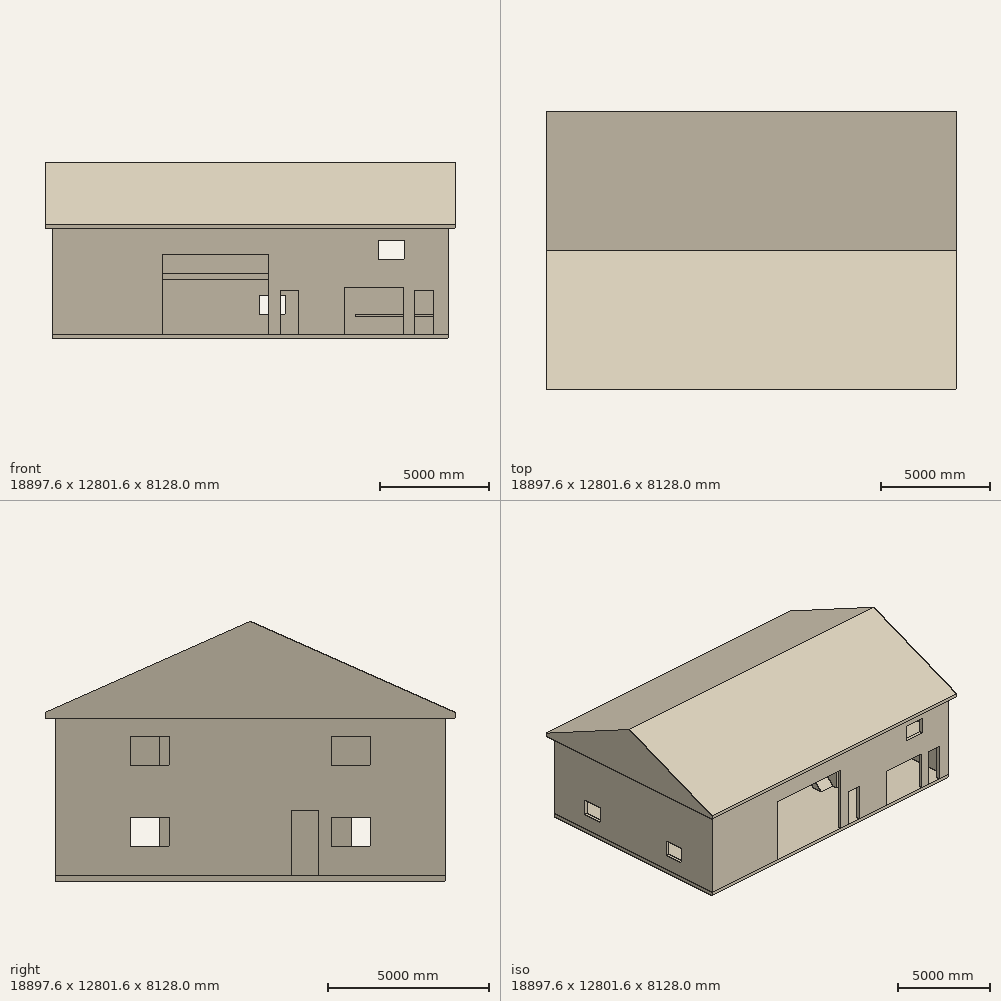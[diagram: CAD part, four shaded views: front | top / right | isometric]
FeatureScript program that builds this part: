
annotation { "Feature Type Name" : "Feature", "Feature Type Description" : "" }
export const myFeature = defineFeature(function(context is Context, id is Id, definition is map)
    precondition{}
    {
        {
            var Q0;
            Q0=qCreatedBy(makeId("Top.planeOp"),FACE);
            var sketch = newSketch(context, id + "F0", { "sketchPlane" : qUnion([Q0])});
            skLineSegment(sketch, "E0.bottom", {"start": v(-9144, 6096) * mm, "end": v(9144, 6096) * mm});
            skLineSegment(sketch, "E0.top", {"start": v(-9144, -6096) * mm, "end": v(9144, -6096) * mm});
            skLineSegment(sketch, "E0.left", {"start": v(-9144, 6096) * mm, "end": v(-9144, -6096) * mm});
            skLineSegment(sketch, "E0.right", {"start": v(9144, 6096) * mm, "end": v(9144, -6096) * mm});
            skLineSegment(sketch, "E1", {"start": v(-9144, 6096) * mm, "end": v(9144, -6096) * mm, "construction": true});
            skSolve(sketch);
        }
        {
            var Q0;
            Q0=makeQuery(id+"F0.imprint","IMPRINT",FACE,{"disambiguationData":[TD([[makeQuery(id+"F0.imprint","IMPRINT",EDGE,{"derivedFrom":sQuery(id+"F0.wireOp",EDGE,"E0.bottom")}),-1.0]])]});
            extrude(context, id + "F1", {"entities" : qUnion([Q0]), "depth" : 203.2 * mm, "offsetDistance" : 25.4 * mm});
        }
        {
            var Q0;
            Q0=makeQuery(id+"F1.opExtrude","CAP_FACE",FACE,{"disambiguationData":[OSD([sQuery(id+"F0.wireOp",EDGE,"E0.bottom"),sQuery(id+"F0.wireOp",EDGE,"E0.top"),sQuery(id+"F0.wireOp",EDGE,"E0.left"),sQuery(id+"F0.wireOp",EDGE,"E0.right")])],"isStart":false});
            var sketch = newSketch(context, id + "F2", { "sketchPlane" : qUnion([Q0])});
            skLineSegment(sketch, "E2.0", {"start": v(-9144, 6096) * mm, "end": v(9144, 6096) * mm});
            skLineSegment(sketch, "E2.1", {"start": v(-9144, 6096) * mm, "end": v(-9144, -6096) * mm});
            skLineSegment(sketch, "E2.2", {"start": v(-9144, -6096) * mm, "end": v(9144, -6096) * mm});
            skLineSegment(sketch, "E2.3", {"start": v(9144, 6096) * mm, "end": v(9144, -6096) * mm});
            skLineSegment(sketch, "E3.0", {"start": v(-8940.8, 5892.8) * mm, "end": v(8940.8, 5892.8) * mm});
            skLineSegment(sketch, "E3.1", {"start": v(-8940.8, 5892.8) * mm, "end": v(-8940.8, -5892.8) * mm});
            skLineSegment(sketch, "E3.2", {"start": v(-8940.8, -5892.8) * mm, "end": v(8940.8, -5892.8) * mm});
            skLineSegment(sketch, "E3.3", {"start": v(8940.8, 5892.8) * mm, "end": v(8940.8, -5892.8) * mm});
            skSolve(sketch);
        }
        {
            var Q0;
            Q0 = qSketchRegion(id + "F2", true);
            extrude(context, id + "F3", {"entities" : qUnion([Q0]), "depth" : 4876.8 * mm, "offsetDistance" : 25.4 * mm});
        }
        {
            var Q0;
            Q0=qCreatedBy(makeId("Right.planeOp"),FACE);
            var sketch = newSketch(context, id + "F4", { "sketchPlane" : qUnion([Q0])});
            skLineSegment(sketch, "E4.0", {"start": v(6400.8, 5080) * mm, "end": v(-6400.8, 5080) * mm});
            skLineSegment(sketch, "E5", {"start": v(-6400.8, 5080) * mm, "end": v(-6400.8, 5283.2) * mm});
            skLineSegment(sketch, "E6", {"start": v(-6400.8, 5283.2) * mm, "end": v(0, 8128) * mm});
            skLineSegment(sketch, "E7", {"start": v(0, 8128) * mm, "end": v(6400.8, 5283.2) * mm});
            skLineSegment(sketch, "E8", {"start": v(6400.8, 5283.2) * mm, "end": v(6400.8, 5080) * mm});
            skSolve(sketch);
        }
        {
            var Q0;
            Q0 = qSketchRegion(id + "F4", true);
            var Q1;
            Q1=makeQuery(id+"F3.opExtrude","SWEPT_FACE",FACE,{"disambiguationData":[OSD([sQuery(id+"F2.wireOp",EDGE,"E2.3")])]});
            var Q2;
            Q2=makeQuery(id+"F3.opExtrude","SWEPT_FACE",FACE,{"disambiguationData":[OSD([sQuery(id+"F2.wireOp",EDGE,"E2.1")])]});
            extrude(context, id + "F5", {"entities" : qUnion([Q0]), "endBound" : BoundingType.UP_TO_SURFACE, "depth" : 25.4 * mm, "endBoundEntityFace" : qUnion([Q1]), "hasOffset" : true, "offsetDistance" : -304.8 * mm, "hasSecondDirection" : true, "secondDirectionBound" : SecondDirectionBoundingType.UP_TO_SURFACE, "secondDirectionOppositeDirection" : true, "secondDirectionDepth" : 25.4 * mm, "secondDirectionBoundEntityFace" : qUnion([Q2]), "hasSecondDirectionOffset" : true, "secondDirectionOffsetDistance" : -304.8 * mm});
        }
        {
            var Q0;
            Q0=makeQuery(id+"F1.opExtrude","CAP_FACE",FACE,{"disambiguationData":[OSD([sQuery(id+"F0.wireOp",EDGE,"E0.bottom"),sQuery(id+"F0.wireOp",EDGE,"E0.top"),sQuery(id+"F0.wireOp",EDGE,"E0.left"),sQuery(id+"F0.wireOp",EDGE,"E0.right")])],"isStart":false});
            var sketch = newSketch(context, id + "F6", { "sketchPlane" : qUnion([Q0])});
            skLineSegment(sketch, "E9", {"start": v(3759.2, -5892.8) * mm, "end": v(3759.2, 5892.8) * mm});
            skLineSegment(sketch, "E10.0", {"start": v(3911.6, -5892.8) * mm, "end": v(3911.6, 203.2) * mm});
            skLineSegment(sketch, "E11", {"start": v(3911.6, 355.6) * mm, "end": v(8940.8, 355.6) * mm});
            skLineSegment(sketch, "E12.0", {"start": v(3911.6, 203.2) * mm, "end": v(8940.8, 203.2) * mm});
            skLineSegment(sketch, "E13.trimOffspring", {"start": v(3911.6, 355.6) * mm, "end": v(3911.6, 5892.8) * mm});
            skLineSegment(sketch, "E14", {"start": v(3759.2, -5892.8) * mm, "end": v(3911.6, -5892.8) * mm});
            skLineSegment(sketch, "E15", {"start": v(3759.2, 5892.8) * mm, "end": v(3911.6, 5892.8) * mm});
            skLineSegment(sketch, "E16", {"start": v(8940.8, 355.6) * mm, "end": v(8940.8, 203.2) * mm});
            skSolve(sketch);
        }
        {
            var Q0;
            Q0 = qSketchRegion(id + "F6", true);
            extrude(context, id + "F7", {"entities" : qUnion([Q0]), "depth" : 2336.8 * mm, "offsetDistance" : 25.4 * mm});
        }
        {
            var Q0;
            Q0=makeQuery(id+"F7.opExtrude","CAP_FACE",FACE,{"disambiguationData":[OSD([sQuery(id+"F6.wireOp",EDGE,"E9"),sQuery(id+"F6.wireOp",EDGE,"E10.0"),sQuery(id+"F6.wireOp",EDGE,"E11"),sQuery(id+"F6.wireOp",EDGE,"E12.0"),sQuery(id+"F6.wireOp",EDGE,"E13.trimOffspring"),sQuery(id+"F6.wireOp",EDGE,"E14"),sQuery(id+"F6.wireOp",EDGE,"E15"),sQuery(id+"F6.wireOp",EDGE,"E16")])],"isStart":false});
            var sketch = newSketch(context, id + "F8", { "sketchPlane" : qUnion([Q0])});
            skLineSegment(sketch, "E17.0", {"start": v(3759.2, -5892.8) * mm, "end": v(3759.2, 5892.8) * mm});
            skLineSegment(sketch, "E18.0", {"start": v(8940.8, 5892.8) * mm, "end": v(8940.8, -5892.8) * mm});
            skLineSegment(sketch, "E19.0", {"start": v(3759.2, 5892.8) * mm, "end": v(8940.8, 5892.8) * mm});
            skLineSegment(sketch, "E20.0", {"start": v(3759.2, -5892.8) * mm, "end": v(8940.8, -5892.8) * mm});
            skPoint(sketch, "E21.orphan", {"position": v(-8940.8, -5892.8) * mm});
            skPoint(sketch, "E22.orphan", {"position": v(-8940.8, 5892.8) * mm});
            skSolve(sketch);
        }
        {
            var Q0;
            Q0 = qSketchRegion(id + "F8", true);
            extrude(context, id + "F9", {"entities" : qUnion([Q0]), "depth" : 203.2 * mm, "offsetDistance" : 25.4 * mm});
        }
        {
            var Q0;
            Q0=makeQuery(id+"F3.opExtrude","SWEPT_FACE",FACE,{"disambiguationData":[OSD([sQuery(id+"F2.wireOp",EDGE,"E2.2")])]});
            var sketch = newSketch(context, id + "F10", { "sketchPlane" : qUnion([Q0])});
            skLineSegment(sketch, "E23.bottom", {"start": v(-4064, 203.2) * mm, "end": v(812.8, 203.2) * mm});
            skLineSegment(sketch, "E23.top", {"start": v(-4064, 3860.8) * mm, "end": v(812.8, 3860.8) * mm});
            skLineSegment(sketch, "E23.left", {"start": v(-4064, 203.2) * mm, "end": v(-4064, 3860.8) * mm});
            skLineSegment(sketch, "E23.right", {"start": v(812.8, 203.2) * mm, "end": v(812.8, 3860.8) * mm});
            skLineSegment(sketch, "E24.bottom", {"start": v(1371.6, 203.2) * mm, "end": v(2235.2, 203.2) * mm});
            skLineSegment(sketch, "E24.top", {"start": v(1371.6, 2235.2) * mm, "end": v(2235.2, 2235.2) * mm});
            skLineSegment(sketch, "E24.left", {"start": v(1371.6, 203.2) * mm, "end": v(1371.6, 2235.2) * mm});
            skLineSegment(sketch, "E24.right", {"start": v(2235.2, 203.2) * mm, "end": v(2235.2, 2235.2) * mm});
            skLineSegment(sketch, "E25.bottom", {"start": v(4318, 203.2) * mm, "end": v(7061.2, 203.2) * mm});
            skLineSegment(sketch, "E25.top", {"start": v(4318, 2336.8) * mm, "end": v(7061.2, 2336.8) * mm});
            skLineSegment(sketch, "E25.left", {"start": v(4318, 203.2) * mm, "end": v(4318, 2336.8) * mm});
            skLineSegment(sketch, "E25.right", {"start": v(7061.2, 203.2) * mm, "end": v(7061.2, 2336.8) * mm});
            skLineSegment(sketch, "E26.bottom", {"start": v(7569.2, 203.2) * mm, "end": v(8432.8, 203.2) * mm});
            skLineSegment(sketch, "E26.top", {"start": v(7569.2, 2235.2) * mm, "end": v(8432.8, 2235.2) * mm});
            skLineSegment(sketch, "E26.left", {"start": v(7569.2, 203.2) * mm, "end": v(7569.2, 2235.2) * mm});
            skLineSegment(sketch, "E26.right", {"start": v(8432.8, 203.2) * mm, "end": v(8432.8, 2235.2) * mm});
            skLineSegment(sketch, "E27.bottom", {"start": v(5892.8, 4546.6) * mm, "end": v(7112, 4546.6) * mm});
            skLineSegment(sketch, "E27.top", {"start": v(5892.8, 3632.2) * mm, "end": v(7112, 3632.2) * mm});
            skLineSegment(sketch, "E27.left", {"start": v(5892.8, 4546.6) * mm, "end": v(5892.8, 3632.2) * mm});
            skLineSegment(sketch, "E27.right", {"start": v(7112, 4546.6) * mm, "end": v(7112, 3632.2) * mm});
            skSolve(sketch);
        }
        {
            var Q0;
            Q0 = qSketchRegion(id + "F10", true);
            extrude(context, id + "F11", {"entities" : qUnion([Q0]), "operationType" : NewBodyOperationType.REMOVE, "endBound" : BoundingType.UP_TO_NEXT, "oppositeDirection" : true, "depth" : 25.4 * mm, "offsetDistance" : 25.4 * mm});
        }
        {
            var Q0;
            Q0=makeQuery(id+"F3.opExtrude","SWEPT_FACE",FACE,{"disambiguationData":[OSD([sQuery(id+"F2.wireOp",EDGE,"E2.3")])]});
            var sketch = newSketch(context, id + "F12", { "sketchPlane" : qUnion([Q0])});
            skLineSegment(sketch, "E28.bottom", {"start": v(-5588, 203.2) * mm, "end": v(-4724.4, 203.2) * mm, "construction": true});
            skLineSegment(sketch, "E28.top", {"start": v(-5588, 2235.2) * mm, "end": v(-4724.4, 2235.2) * mm, "construction": true});
            skLineSegment(sketch, "E28.left", {"start": v(-5588, 203.2) * mm, "end": v(-5588, 2235.2) * mm, "construction": true});
            skLineSegment(sketch, "E28.right", {"start": v(-4724.4, 203.2) * mm, "end": v(-4724.4, 2235.2) * mm, "construction": true});
            skLineSegment(sketch, "E29.bottom", {"start": v(1270, 203.2) * mm, "end": v(2133.6, 203.2) * mm});
            skLineSegment(sketch, "E29.top", {"start": v(1270, 2235.2) * mm, "end": v(2133.6, 2235.2) * mm});
            skLineSegment(sketch, "E29.left", {"start": v(1270, 203.2) * mm, "end": v(1270, 2235.2) * mm});
            skLineSegment(sketch, "E29.right", {"start": v(2133.6, 203.2) * mm, "end": v(2133.6, 2235.2) * mm});
            skSolve(sketch);
        }
        {
            var Q0;
            Q0 = qSketchRegion(id + "F12", true);
            extrude(context, id + "F13", {"entities" : qUnion([Q0]), "operationType" : NewBodyOperationType.REMOVE, "endBound" : BoundingType.UP_TO_NEXT, "oppositeDirection" : true, "depth" : 25.4 * mm, "offsetDistance" : 25.4 * mm});
        }
        {
            var Q0;
            Q0=makeQuery(id+"F7.opExtrude","SWEPT_FACE",FACE,{"disambiguationData":[OSD([sQuery(id+"F6.wireOp",EDGE,"E9")])]});
            var sketch = newSketch(context, id + "F14", { "sketchPlane" : qUnion([Q0])});
            skLineSegment(sketch, "E30", {"start": v(1965.26, 203.2) * mm, "end": v(-371.54, 2540) * mm});
            skLineSegment(sketch, "E31", {"start": v(0, 2743.2) * mm, "end": v(2540, 203.2) * mm});
            skLineSegment(sketch, "E32", {"start": v(-574.74, 2743.2) * mm, "end": v(0, 2743.2) * mm});
            skLineSegment(sketch, "E33", {"start": v(2540, 203.2) * mm, "end": v(1965.26, 203.2) * mm});
            skLineSegment(sketch, "E34.bottom", {"start": v(2955.8, 203.2) * mm, "end": v(5394.2, 203.2) * mm, "construction": true});
            skLineSegment(sketch, "E34.top", {"start": v(2955.8, 2336.8) * mm, "end": v(5394.2, 2336.8) * mm, "construction": true});
            skLineSegment(sketch, "E34.left", {"start": v(2955.8, 203.2) * mm, "end": v(2955.8, 2336.8) * mm, "construction": true});
            skLineSegment(sketch, "E34.right", {"start": v(5394.2, 203.2) * mm, "end": v(5394.2, 2336.8) * mm, "construction": true});
            skLineSegment(sketch, "E35.bottom", {"start": v(-4403.76, 203.2) * mm, "end": v(-1965.36, 203.2) * mm, "construction": true});
            skLineSegment(sketch, "E35.top", {"start": v(-4403.76, 2336.8) * mm, "end": v(-1965.36, 2336.8) * mm, "construction": true});
            skLineSegment(sketch, "E35.left", {"start": v(-4403.76, 203.2) * mm, "end": v(-4403.76, 2336.8) * mm, "construction": true});
            skLineSegment(sketch, "E35.right", {"start": v(-1965.36, 203.2) * mm, "end": v(-1965.36, 2336.8) * mm, "construction": true});
            skLineSegment(sketch, "E36", {"start": v(-1219.2, 2540) * mm, "end": v(-1219.2, 2743.2) * mm});
            skLineSegment(sketch, "E37", {"start": v(-1219.2, 2743.2) * mm, "end": v(-574.74, 2743.2) * mm});
            skLineSegment(sketch, "E38", {"start": v(-1219.2, 2540) * mm, "end": v(-371.54, 2540) * mm});
            skSolve(sketch);
        }
        {
            var Q0;
            Q0 = qSketchRegion(id + "F14", true);
            extrude(context, id + "F15", {"entities" : qUnion([Q0]), "depth" : 914.4 * mm, "offsetDistance" : 25.4 * mm});
        }
        {
            var Q0;
            Q0=makeQuery(id+"F7.opExtrude","SWEPT_FACE",FACE,{"disambiguationData":[OSD([sQuery(id+"F6.wireOp",EDGE,"E9")])]});
            var sketch = newSketch(context, id + "F16", { "sketchPlane" : qUnion([Q0])});
            skLineSegment(sketch, "E39.bottom", {"start": v(-5588, 203.2) * mm, "end": v(-3149.6, 203.2) * mm});
            skLineSegment(sketch, "E39.top", {"start": v(-5588, 2336.8) * mm, "end": v(-3149.6, 2336.8) * mm});
            skLineSegment(sketch, "E39.left", {"start": v(-5588, 203.2) * mm, "end": v(-5588, 2336.8) * mm});
            skLineSegment(sketch, "E39.right", {"start": v(-3149.6, 203.2) * mm, "end": v(-3149.6, 2336.8) * mm});
            skLineSegment(sketch, "E40.bottom", {"start": v(2844.8, 203.2) * mm, "end": v(5283.2, 203.2) * mm});
            skLineSegment(sketch, "E40.top", {"start": v(2844.8, 2336.8) * mm, "end": v(5283.2, 2336.8) * mm});
            skLineSegment(sketch, "E40.left", {"start": v(2844.8, 203.2) * mm, "end": v(2844.8, 2336.8) * mm});
            skLineSegment(sketch, "E40.right", {"start": v(5283.2, 203.2) * mm, "end": v(5283.2, 2336.8) * mm});
            skSolve(sketch);
        }
        {
            var Q0;
            Q0 = qSketchRegion(id + "F16", true);
            extrude(context, id + "F17", {"entities" : qUnion([Q0]), "operationType" : NewBodyOperationType.REMOVE, "endBound" : BoundingType.UP_TO_NEXT, "oppositeDirection" : true, "depth" : 25.4 * mm, "offsetDistance" : 25.4 * mm});
        }
        {
            var Q0;
            Q0=makeQuery(id+"F9.opExtrude","CAP_FACE",FACE,{"disambiguationData":[OSD([sQuery(id+"F8.wireOp",EDGE,"E17.0"),sQuery(id+"F8.wireOp",EDGE,"E18.0"),sQuery(id+"F8.wireOp",EDGE,"E19.0"),sQuery(id+"F8.wireOp",EDGE,"E20.0")])],"isStart":false});
            var sketch = newSketch(context, id + "F18", { "sketchPlane" : qUnion([Q0])});
            skLineSegment(sketch, "E41.0", {"start": v(3759.2, -5892.8) * mm, "end": v(3759.2, 5892.8) * mm});
            skLineSegment(sketch, "E42.0", {"start": v(3911.6, -5892.8) * mm, "end": v(3911.6, 5892.8) * mm});
            skLineSegment(sketch, "E43", {"start": v(3759.2, 5892.8) * mm, "end": v(3911.6, 5892.8) * mm});
            skLineSegment(sketch, "E44", {"start": v(3759.2, -5892.8) * mm, "end": v(3911.6, -5892.8) * mm});
            skSolve(sketch);
        }
        {
            var Q0;
            Q0 = qSketchRegion(id + "F18", true);
            var Q1;
            Q1=makeQuery(id+"F3.opExtrude","CAP_FACE",FACE,{"disambiguationData":[OSD([sQuery(id+"F2.wireOp",EDGE,"E2.0"),sQuery(id+"F2.wireOp",EDGE,"E2.1"),sQuery(id+"F2.wireOp",EDGE,"E2.2"),sQuery(id+"F2.wireOp",EDGE,"E2.3"),sQuery(id+"F2.wireOp",EDGE,"E3.0"),sQuery(id+"F2.wireOp",EDGE,"E3.1"),sQuery(id+"F2.wireOp",EDGE,"E3.2"),sQuery(id+"F2.wireOp",EDGE,"E3.3")])],"isStart":false});
            extrude(context, id + "F19", {"entities" : qUnion([Q0]), "endBound" : BoundingType.UP_TO_SURFACE, "depth" : 25.4 * mm, "endBoundEntityFace" : qUnion([Q1]), "offsetDistance" : 25.4 * mm});
        }
        {
            var Q0;
            Q0=makeQuery(id+"F19.opExtrude","SWEPT_FACE",FACE,{"disambiguationData":[OSD([sQuery(id+"F18.wireOp",EDGE,"E41.0")])]});
            var sketch = newSketch(context, id + "F20", { "sketchPlane" : qUnion([Q0])});
            skLineSegment(sketch, "E45.bottom", {"start": v(-1219.2, 2743.2) * mm, "end": v(-355.6, 2743.2) * mm});
            skLineSegment(sketch, "E45.top", {"start": v(-1219.2, 4724.4) * mm, "end": v(-355.6, 4724.4) * mm});
            skLineSegment(sketch, "E45.left", {"start": v(-1219.2, 2743.2) * mm, "end": v(-1219.2, 4724.4) * mm});
            skLineSegment(sketch, "E45.right", {"start": v(-355.6, 2743.2) * mm, "end": v(-355.6, 4724.4) * mm});
            skLineSegment(sketch, "E46.bottom", {"start": v(2844.8, 2743.2) * mm, "end": v(5283.2, 2743.2) * mm});
            skLineSegment(sketch, "E46.top", {"start": v(2844.8, 4724.4) * mm, "end": v(5283.2, 4724.4) * mm});
            skLineSegment(sketch, "E46.left", {"start": v(2844.8, 2743.2) * mm, "end": v(2844.8, 4724.4) * mm});
            skLineSegment(sketch, "E46.right", {"start": v(5283.2, 2743.2) * mm, "end": v(5283.2, 4724.4) * mm});
            skSolve(sketch);
        }
        {
            var Q0;
            Q0 = qSketchRegion(id + "F20", true);
            extrude(context, id + "F21", {"entities" : qUnion([Q0]), "operationType" : NewBodyOperationType.REMOVE, "endBound" : BoundingType.UP_TO_NEXT, "oppositeDirection" : true, "depth" : 25.4 * mm, "offsetDistance" : 25.4 * mm});
        }
        {
            var Q0;
            Q0=makeQuery(id+"F3.opExtrude","SWEPT_FACE",FACE,{"disambiguationData":[OSD([sQuery(id+"F2.wireOp",EDGE,"E3.0")])]});
            var sketch = newSketch(context, id + "F22", { "sketchPlane" : qUnion([Q0])});
            skLineSegment(sketch, "E47.bottom", {"start": v(-8940.8, 2997.2) * mm, "end": v(3759.2, 2997.2) * mm});
            skLineSegment(sketch, "E47.top", {"start": v(-8940.8, 2743.2) * mm, "end": v(3759.2, 2743.2) * mm});
            skLineSegment(sketch, "E47.left", {"start": v(-8940.8, 2997.2) * mm, "end": v(-8940.8, 2743.2) * mm});
            skLineSegment(sketch, "E47.right", {"start": v(3759.2, 2997.2) * mm, "end": v(3759.2, 2743.2) * mm});
            skSolve(sketch);
        }
        {
            var Q0;
            Q0 = qSketchRegion(id + "F22", true);
            extrude(context, id + "F23", {"entities" : qUnion([Q0]), "depth" : 4572 * mm, "offsetDistance" : 25.4 * mm});
        }
        {
            var Q0;
            Q0=makeQuery(id+"F3.opExtrude","SWEPT_FACE",FACE,{"disambiguationData":[OSD([sQuery(id+"F2.wireOp",EDGE,"E3.1")])]});
            var sketch = newSketch(context, id + "F24", { "sketchPlane" : qUnion([Q0])});
            skLineSegment(sketch, "E48.bottom", {"start": v(5892.8, 3225.8) * mm, "end": v(-4064, 3225.8) * mm});
            skLineSegment(sketch, "E48.top", {"start": v(5892.8, 2971.8) * mm, "end": v(-4064, 2971.8) * mm});
            skLineSegment(sketch, "E48.left", {"start": v(5892.8, 3225.8) * mm, "end": v(5892.8, 2971.8) * mm});
            skLineSegment(sketch, "E48.right", {"start": v(-4064, 3225.8) * mm, "end": v(-4064, 2971.8) * mm});
            skSolve(sketch);
        }
        {
            var Q0;
            Q0 = qSketchRegion(id + "F24", true);
            extrude(context, id + "F25", {"entities" : qUnion([Q0]), "depth" : 4876.8 * mm, "offsetDistance" : 25.4 * mm});
        }
        {
            var Q0;
            Q0=makeQuery(id+"F7.opExtrude","SWEPT_FACE",FACE,{"disambiguationData":[OSD([sQuery(id+"F6.wireOp",EDGE,"E11")])]});
            var sketch = newSketch(context, id + "F26", { "sketchPlane" : qUnion([Q0])});
            skLineSegment(sketch, "E49.bottom", {"start": v(-8940.8, 1879.6) * mm, "end": v(-3911.6, 1879.6) * mm});
            skLineSegment(sketch, "E49.top", {"start": v(-8940.8, 1828.8) * mm, "end": v(-3911.6, 1828.8) * mm});
            skLineSegment(sketch, "E49.left", {"start": v(-8940.8, 1879.6) * mm, "end": v(-8940.8, 1828.8) * mm});
            skLineSegment(sketch, "E49.right", {"start": v(-3911.6, 1879.6) * mm, "end": v(-3911.6, 1828.8) * mm});
            skLineSegment(sketch, "E50.bottom", {"start": v(-8940.8, 1320.8) * mm, "end": v(-3911.6, 1320.8) * mm});
            skLineSegment(sketch, "E50.top", {"start": v(-8940.8, 1270) * mm, "end": v(-3911.6, 1270) * mm});
            skLineSegment(sketch, "E50.left", {"start": v(-8940.8, 1320.8) * mm, "end": v(-8940.8, 1270) * mm});
            skLineSegment(sketch, "E50.right", {"start": v(-3911.6, 1320.8) * mm, "end": v(-3911.6, 1270) * mm});
            skLineSegment(sketch, "E51.bottom", {"start": v(-8940.8, 762) * mm, "end": v(-3911.6, 762) * mm});
            skLineSegment(sketch, "E51.top", {"start": v(-8940.8, 711.2) * mm, "end": v(-3911.6, 711.2) * mm});
            skLineSegment(sketch, "E51.left", {"start": v(-8940.8, 762) * mm, "end": v(-8940.8, 711.2) * mm});
            skLineSegment(sketch, "E51.right", {"start": v(-3911.6, 762) * mm, "end": v(-3911.6, 711.2) * mm});
            skSolve(sketch);
        }
        {
            var Q0;
            Q0 = qSketchRegion(id + "F26", true);
            extrude(context, id + "F27", {"entities" : qUnion([Q0]), "operationType" : NewBodyOperationType.ADD, "depth" : 609.6 * mm, "offsetDistance" : 25.4 * mm});
        }
        {
            var Q0;
            Q0=makeQuery(id+"F7.opExtrude","SWEPT_FACE",FACE,{"disambiguationData":[OSD([sQuery(id+"F6.wireOp",EDGE,"E12.0")])]});
            var sketch = newSketch(context, id + "F28", { "sketchPlane" : qUnion([Q0])});
            skLineSegment(sketch, "E52.bottom", {"start": v(4826, 1117.6) * mm, "end": v(8940.8, 1117.6) * mm});
            skLineSegment(sketch, "E52.top", {"start": v(4826, 1041.4) * mm, "end": v(8940.8, 1041.4) * mm});
            skLineSegment(sketch, "E52.left", {"start": v(4826, 1117.6) * mm, "end": v(4826, 1041.4) * mm});
            skLineSegment(sketch, "E52.right", {"start": v(8940.8, 1117.6) * mm, "end": v(8940.8, 1041.4) * mm});
            skSolve(sketch);
        }
        {
            var Q0;
            Q0 = qSketchRegion(id + "F28", true);
            extrude(context, id + "F29", {"entities" : qUnion([Q0]), "operationType" : NewBodyOperationType.ADD, "depth" : 914.4 * mm, "offsetDistance" : 25.4 * mm});
        }
        {
            var Q0;
            Q0=makeQuery(id+"F3.opExtrude","SWEPT_FACE",FACE,{"disambiguationData":[OSD([sQuery(id+"F2.wireOp",EDGE,"E2.0")])]});
            var sketch = newSketch(context, id + "F30", { "sketchPlane" : qUnion([Q0])});
            skLineSegment(sketch, "E53.0", {"start": v(-5892.8, 4546.6) * mm, "end": v(-5892.8, 3632.2) * mm});
            skLineSegment(sketch, "E53.1", {"start": v(-5892.8, 4546.6) * mm, "end": v(-7112, 4546.6) * mm});
            skLineSegment(sketch, "E53.2", {"start": v(-5892.8, 3632.2) * mm, "end": v(-7112, 3632.2) * mm});
            skLineSegment(sketch, "E53.3", {"start": v(-7112, 4546.6) * mm, "end": v(-7112, 3632.2) * mm});
            skLineSegment(sketch, "E54.bottom", {"start": v(-7112, 2006.6) * mm, "end": v(-5892.8, 2006.6) * mm});
            skLineSegment(sketch, "E54.top", {"start": v(-7112, 1092.2) * mm, "end": v(-5892.8, 1092.2) * mm});
            skLineSegment(sketch, "E54.left", {"start": v(-7112, 2006.6) * mm, "end": v(-7112, 1092.2) * mm});
            skLineSegment(sketch, "E54.right", {"start": v(-5892.8, 2006.6) * mm, "end": v(-5892.8, 1092.2) * mm});
            skLineSegment(sketch, "E55.bottom", {"start": v(-1625.6, 2006.6) * mm, "end": v(-406.4, 2006.6) * mm});
            skLineSegment(sketch, "E55.top", {"start": v(-1625.6, 1092.2) * mm, "end": v(-406.4, 1092.2) * mm});
            skLineSegment(sketch, "E55.left", {"start": v(-1625.6, 2006.6) * mm, "end": v(-1625.6, 1092.2) * mm});
            skLineSegment(sketch, "E55.right", {"start": v(-406.4, 2006.6) * mm, "end": v(-406.4, 1092.2) * mm});
            skLineSegment(sketch, "E56.bottom", {"start": v(5588, 2006.6) * mm, "end": v(6807.2, 2006.6) * mm});
            skLineSegment(sketch, "E56.top", {"start": v(5588, 1092.2) * mm, "end": v(6807.2, 1092.2) * mm});
            skLineSegment(sketch, "E56.left", {"start": v(5588, 2006.6) * mm, "end": v(5588, 1092.2) * mm});
            skLineSegment(sketch, "E56.right", {"start": v(6807.2, 2006.6) * mm, "end": v(6807.2, 1092.2) * mm});
            skSolve(sketch);
        }
        {
            var Q0;
            Q0 = qSketchRegion(id + "F30", true);
            extrude(context, id + "F31", {"entities" : qUnion([Q0]), "operationType" : NewBodyOperationType.REMOVE, "endBound" : BoundingType.UP_TO_NEXT, "oppositeDirection" : true, "depth" : 25.4 * mm, "offsetDistance" : 25.4 * mm});
        }
        {
            var Q0;
            Q0=makeQuery(id+"F3.opExtrude","SWEPT_FACE",FACE,{"disambiguationData":[OSD([sQuery(id+"F2.wireOp",EDGE,"E2.1")])]});
            var sketch = newSketch(context, id + "F32", { "sketchPlane" : qUnion([Q0])});
            skLineSegment(sketch, "E57.bottom", {"start": v(-3759.2, 2006.6) * mm, "end": v(-2540, 2006.6) * mm});
            skLineSegment(sketch, "E57.top", {"start": v(-3759.2, 1092.2) * mm, "end": v(-2540, 1092.2) * mm});
            skLineSegment(sketch, "E57.left", {"start": v(-3759.2, 2006.6) * mm, "end": v(-3759.2, 1092.2) * mm});
            skLineSegment(sketch, "E57.right", {"start": v(-2540, 2006.6) * mm, "end": v(-2540, 1092.2) * mm});
            skLineSegment(sketch, "E58.bottom", {"start": v(2540, 2006.6) * mm, "end": v(3759.2, 2006.6) * mm});
            skLineSegment(sketch, "E58.top", {"start": v(2540, 1092.2) * mm, "end": v(3759.2, 1092.2) * mm});
            skLineSegment(sketch, "E58.left", {"start": v(2540, 2006.6) * mm, "end": v(2540, 1092.2) * mm});
            skLineSegment(sketch, "E58.right", {"start": v(3759.2, 2006.6) * mm, "end": v(3759.2, 1092.2) * mm});
            skSolve(sketch);
        }
        {
            var Q0;
            Q0=makeQuery(id+"F32.imprint","IMPRINT",FACE,{"disambiguationData":[TD([[makeQuery(id+"F32.imprint","IMPRINT",EDGE,{"derivedFrom":sQuery(id+"F32.wireOp",EDGE,"E57.bottom")}),-1.0]])]});
            var Q1;
            Q1=makeQuery(id+"F32.imprint","IMPRINT",FACE,{"disambiguationData":[TD([[makeQuery(id+"F32.imprint","IMPRINT",EDGE,{"derivedFrom":sQuery(id+"F32.wireOp",EDGE,"E58.bottom")}),-1.0]])]});
            extrude(context, id + "F33", {"entities" : qUnion([Q0, Q1]), "operationType" : NewBodyOperationType.REMOVE, "endBound" : BoundingType.UP_TO_NEXT, "oppositeDirection" : true, "depth" : 25.4 * mm, "offsetDistance" : 25.4 * mm});
        }
        {
            var Q0;
            Q0=makeQuery(id+"F3.opExtrude","SWEPT_FACE",FACE,{"disambiguationData":[OSD([sQuery(id+"F2.wireOp",EDGE,"E2.3")])]});
            var sketch = newSketch(context, id + "F34", { "sketchPlane" : qUnion([Q0])});
            skLineSegment(sketch, "E59.0", {"start": v(-2540, 2006.6) * mm, "end": v(-3759.2, 2006.6) * mm});
            skLineSegment(sketch, "E59.1", {"start": v(-2540, 2006.6) * mm, "end": v(-2540, 1092.2) * mm});
            skLineSegment(sketch, "E59.2", {"start": v(-2540, 1092.2) * mm, "end": v(-3759.2, 1092.2) * mm});
            skLineSegment(sketch, "E59.3", {"start": v(-3759.2, 2006.6) * mm, "end": v(-3759.2, 1092.2) * mm});
            skLineSegment(sketch, "E59.4", {"start": v(3759.2, 2006.6) * mm, "end": v(2540, 2006.6) * mm});
            skLineSegment(sketch, "E59.5", {"start": v(3759.2, 2006.6) * mm, "end": v(3759.2, 1092.2) * mm});
            skLineSegment(sketch, "E59.6", {"start": v(3759.2, 1092.2) * mm, "end": v(2540, 1092.2) * mm});
            skLineSegment(sketch, "E59.7", {"start": v(2540, 2006.6) * mm, "end": v(2540, 1092.2) * mm});
            skLineSegment(sketch, "E60.bottom", {"start": v(-3759.2, 4546.6) * mm, "end": v(-2540, 4546.6) * mm});
            skLineSegment(sketch, "E60.top", {"start": v(-3759.2, 3632.2) * mm, "end": v(-2540, 3632.2) * mm});
            skLineSegment(sketch, "E60.left", {"start": v(-3759.2, 4546.6) * mm, "end": v(-3759.2, 3632.2) * mm});
            skLineSegment(sketch, "E60.right", {"start": v(-2540, 4546.6) * mm, "end": v(-2540, 3632.2) * mm});
            skLineSegment(sketch, "E61.bottom", {"start": v(2540, 4546.6) * mm, "end": v(3759.2, 4546.6) * mm});
            skLineSegment(sketch, "E61.top", {"start": v(2540, 3632.2) * mm, "end": v(3759.2, 3632.2) * mm});
            skLineSegment(sketch, "E61.left", {"start": v(2540, 4546.6) * mm, "end": v(2540, 3632.2) * mm});
            skLineSegment(sketch, "E61.right", {"start": v(3759.2, 4546.6) * mm, "end": v(3759.2, 3632.2) * mm});
            skSolve(sketch);
        }
        {
            var Q0;
            Q0 = qSketchRegion(id + "F34", true);
            extrude(context, id + "F35", {"entities" : qUnion([Q0]), "operationType" : NewBodyOperationType.REMOVE, "endBound" : BoundingType.UP_TO_NEXT, "oppositeDirection" : true, "depth" : 25.4 * mm, "offsetDistance" : 25.4 * mm});
        }
    });
